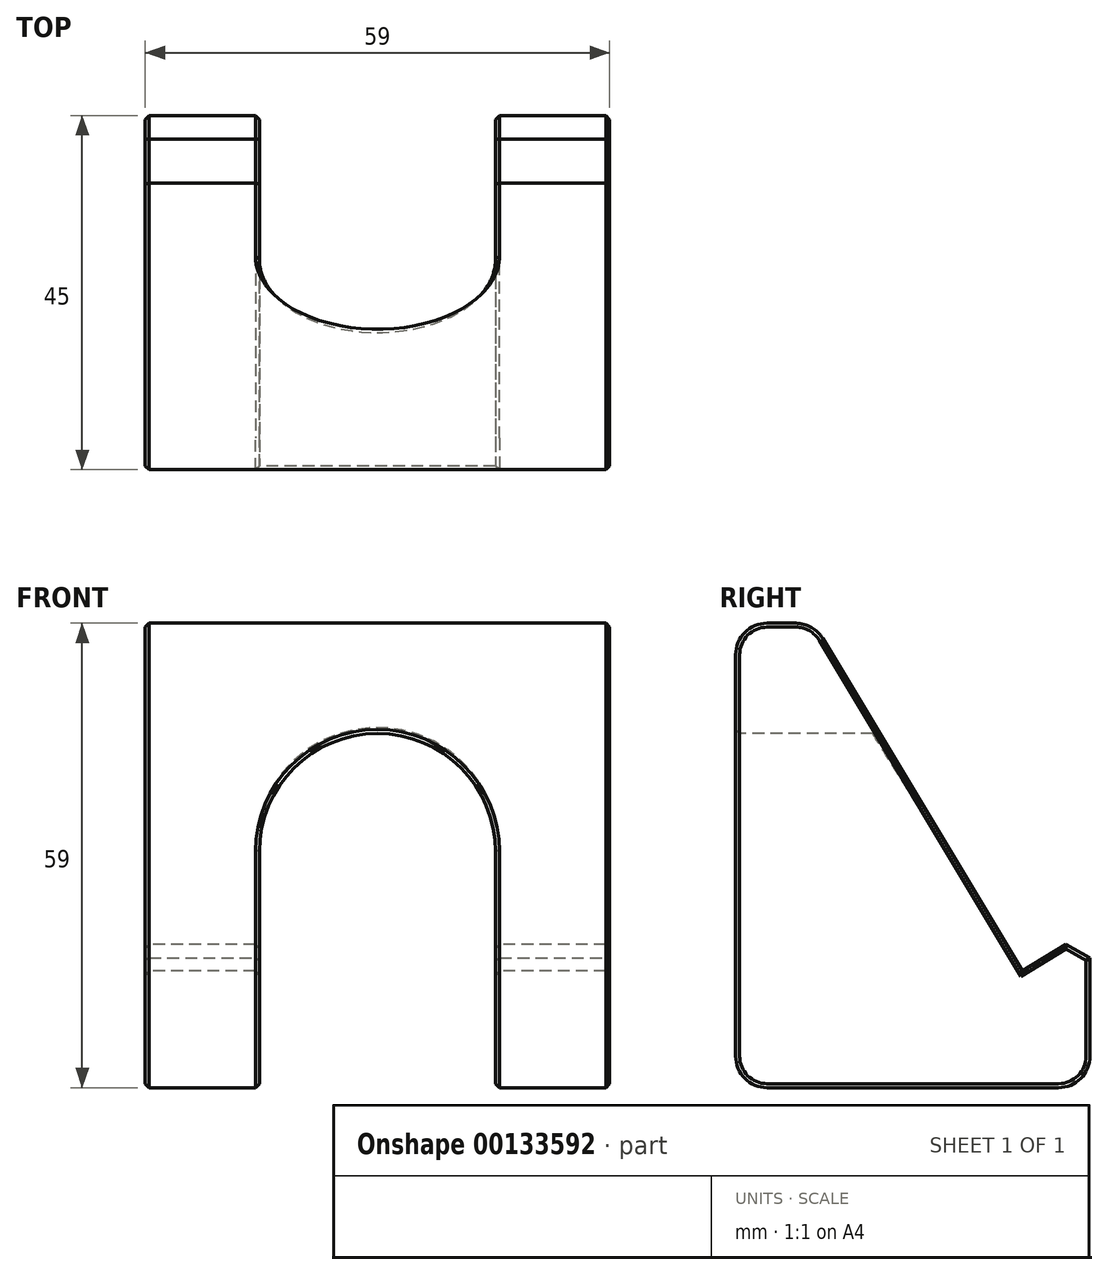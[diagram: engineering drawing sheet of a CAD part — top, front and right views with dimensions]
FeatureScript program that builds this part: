
annotation { "Feature Type Name" : "Feature", "Feature Type Description" : "" }
export const myFeature = defineFeature(function(context is Context, id is Id, definition is map)
    precondition{}
    {
        {
            var Q0;
            Q0=qCreatedBy(makeId("Right.planeOp"),FACE);
            var sketch = newSketch(context, id + "F0", { "sketchPlane" : qUnion([Q0])});
            skLineSegment(sketch, "E0", {"start": v(0, 0) * mm, "end": v(0, 59) * mm});
            skLineSegment(sketch, "E1", {"start": v(0, 59) * mm, "end": v(9.9, 59) * mm});
            skLineSegment(sketch, "E2", {"start": v(45, 20) * mm, "end": v(45, 0) * mm});
            skLineSegment(sketch, "E3", {"start": v(45, 0) * mm, "end": v(0, 0) * mm});
            skLineSegment(sketch, "E4", {"start": v(9.9, 59) * mm, "end": v(36.43, 14.85) * mm});
            skLineSegment(sketch, "E5", {"start": v(36.43, 14.85) * mm, "end": v(45, 20) * mm});
            skSolve(sketch);
        }
        {
            var Q0;
            Q0=makeQuery(id+"F0.imprint","IMPRINT",FACE,{"disambiguationData":[TD([[makeQuery(id+"F0.imprint","IMPRINT",EDGE,{"derivedFrom":sQuery(id+"F0.wireOp",EDGE,"E0")}),-1.0]])]});
            extrude(context, id + "F1", {"entities" : qUnion([Q0]), "endBound" : BoundingType.SYMMETRIC, "depth" : 59 * mm});
        }
        {
            var Q0;
            Q0=makeQuery(id+"F1.opExtrude","SWEPT_EDGE",EDGE,{"disambiguationData":[OSD([sQuery(id+"F0.wireOp",EDGE,"E1"),sQuery(id+"F0.wireOp",EDGE,"E4")])]});
            var Q1;
            Q1=makeQuery(id+"F1.opExtrude","SWEPT_EDGE",EDGE,{"disambiguationData":[OSD([sQuery(id+"F0.wireOp",EDGE,"E0"),sQuery(id+"F0.wireOp",EDGE,"E1")])]});
            var Q2;
            Q2=makeQuery(id+"F1.opExtrude","SWEPT_EDGE",EDGE,{"disambiguationData":[OSD([sQuery(id+"F0.wireOp",EDGE,"E0"),sQuery(id+"F0.wireOp",EDGE,"E3")])]});
            var Q3;
            Q3=makeQuery(id+"F1.opExtrude","SWEPT_EDGE",EDGE,{"disambiguationData":[OSD([sQuery(id+"F0.wireOp",EDGE,"E2"),sQuery(id+"F0.wireOp",EDGE,"E3")])]});
            fillet(context, id + "F2", {"entities" : qUnion([Q0, Q1, Q2, Q3]), "radius" : 4 * mm, "tangentPropagation" : true, "allowEdgeOverflow" : false});
        }
        {
            var Q0;
            Q0=makeQuery(id+"F1.opExtrude","SWEPT_EDGE",EDGE,{"disambiguationData":[OSD([sQuery(id+"F0.wireOp",EDGE,"E2"),sQuery(id+"F0.wireOp",EDGE,"E5")])]});
            chamfer(context, id + "F3", {"entities" : qUnion([Q0]), "width" : 2 * mm, "tangentPropagation" : true});
        }
        {
            var Q0;
            Q0=makeQuery(id+"F1.opExtrude","SWEPT_FACE",FACE,{"disambiguationData":[OSD([sQuery(id+"F0.wireOp",EDGE,"E0")])]});
            var sketch = newSketch(context, id + "F4", { "sketchPlane" : qUnion([Q0])});
            skArc(sketch, "E6", {"start": v(15, 30) * mm, "mid": v(0, 45) * mm, "end": v(-15, 30) * mm});
            skLineSegment(sketch, "E7", {"start": v(15, 30) * mm, "end": v(15, 0) * mm});
            skLineSegment(sketch, "E8", {"start": v(15, 0) * mm, "end": v(-15, 0) * mm});
            skLineSegment(sketch, "E9", {"start": v(-15, 0) * mm, "end": v(-15, 30) * mm});
            skSolve(sketch);
        }
        {
            var Q0;
            {var subQ0=sQuery(id+"F4.wireOp",EDGE,"E6");Q0=makeQuery(id+"F4.imprint","IMPRINT",FACE,{"disambiguationData":[TD([[makeQuery(id+"F4.imprint","IMPRINT",EDGE,{"derivedFrom":subQ0}),1.0]])]});}
            var Q1;
            {var subQ0=sQuery(id+"F4.wireOp",EDGE,"E8");Q1=makeQuery(id+"F4.imprint","IMPRINT",FACE,{"disambiguationData":[TD([[makeQuery(id+"F4.imprint","IMPRINT",EDGE,{"derivedFrom":subQ0}),-1.0]])]});}
            extrude(context, id + "F5", {"entities" : qUnion([Q0, Q1]), "operationType" : NewBodyOperationType.REMOVE, "endBound" : BoundingType.THROUGH_ALL, "oppositeDirection" : true, "depth" : 25 * mm});
        }
        {
            var Q0;
            Q0=makeQuery(id+"F1.opExtrude","CAP_FACE",FACE,{"disambiguationData":[OSD([sQuery(id+"F0.wireOp",EDGE,"E0"),sQuery(id+"F0.wireOp",EDGE,"E1"),sQuery(id+"F0.wireOp",EDGE,"E2"),sQuery(id+"F0.wireOp",EDGE,"E3"),sQuery(id+"F0.wireOp",EDGE,"E4"),sQuery(id+"F0.wireOp",EDGE,"E5")])],"isStart":true});
            var Q1;
            Q1=makeQuery(id+"F1.opExtrude","CAP_FACE",FACE,{"disambiguationData":[OSD([sQuery(id+"F0.wireOp",EDGE,"E0"),sQuery(id+"F0.wireOp",EDGE,"E1"),sQuery(id+"F0.wireOp",EDGE,"E2"),sQuery(id+"F0.wireOp",EDGE,"E3"),sQuery(id+"F0.wireOp",EDGE,"E4"),sQuery(id+"F0.wireOp",EDGE,"E5")])],"isStart":false});
            var Q2;
            Q2=makeQuery(id+"F5.boolean.opBoolean","COPY",FACE,{"derivedFrom":makeQuery(id+"F5.opExtrude","SWEPT_FACE",FACE,{"disambiguationData":[OSD([sQuery(id+"F4.wireOp",EDGE,"E7")])]})});
            var Q3;
            Q3=makeQuery(id+"F5.boolean.opBoolean","COPY",FACE,{"derivedFrom":makeQuery(id+"F5.opExtrude","SWEPT_FACE",FACE,{"disambiguationData":[OSD([sQuery(id+"F4.wireOp",EDGE,"E6")])]})});
            var Q4;
            Q4=makeQuery(id+"F5.boolean.opBoolean","COPY",FACE,{"derivedFrom":makeQuery(id+"F5.opExtrude","SWEPT_FACE",FACE,{"disambiguationData":[OSD([sQuery(id+"F4.wireOp",EDGE,"E9")])]})});
            chamfer(context, id + "F6", {"entities" : qUnion([Q0, Q1, Q2, Q3, Q4]), "width" : .5 * mm, "tangentPropagation" : true});
        }
    });
